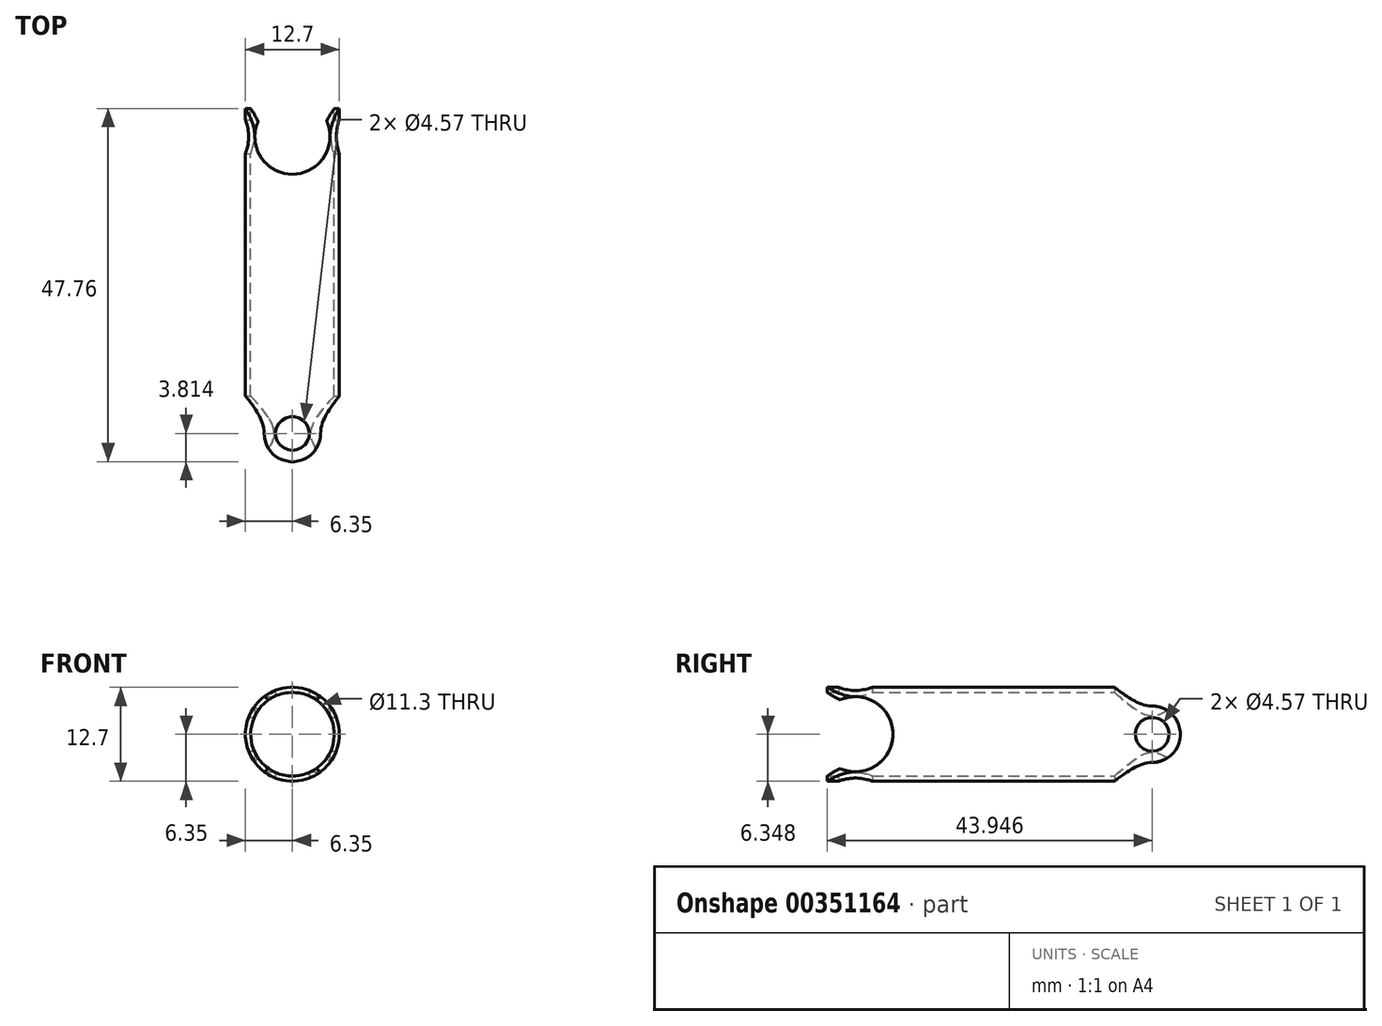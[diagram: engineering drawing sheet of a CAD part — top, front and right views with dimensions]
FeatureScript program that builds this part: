
annotation { "Feature Type Name" : "Feature", "Feature Type Description" : "" }
export const myFeature = defineFeature(function(context is Context, id is Id, definition is map)
    precondition{}
    {
        {
            var Q0;
            Q0=qCreatedBy(makeId("Front.planeOp"),FACE);
            var sketch = newSketch(context, id + "F0", { "sketchPlane" : qUnion([Q0])});
            skCircle(sketch, "E0", {"center": v(0, 0) * mm, "radius": 6.35 * mm});
            skCircle(sketch, "E1", {"center": v(0, 0) * mm, "radius": 5.65 * mm});
            skSolve(sketch);
        }
        {
            var Q0;
            Q0 = qSketchRegion(id + "F0", true);
            extrude(context, id + "F1", {"entities" : qUnion([Q0]), "depth" : 50.8 * mm});
        }
        {
            var Q0;
            Q0=qCreatedBy(makeId("Right.planeOp"),FACE);
            var sketch = newSketch(context, id + "F2", { "sketchPlane" : qUnion([Q0])});
            skCircle(sketch, "E2", {"center": v(-45.47, 0) * mm, "radius": 5.08 * mm});
            skCircle(sketch, "E3", {"center": v(-5.33, 0) * mm, "radius": 2.29 * mm});
            skSolve(sketch);
        }
        {
            var Q0;
            Q0 = qSketchRegion(id + "F2", true);
            extrude(context, id + "F3", {"entities" : qUnion([Q0]), "operationType" : NewBodyOperationType.REMOVE, "endBound" : BoundingType.SYMMETRIC, "oppositeDirection" : true, "depth" : 25.4 * mm});
        }
        {
            var Q0;
            Q0=qCreatedBy(makeId("Top.planeOp"),FACE);
            var sketch = newSketch(context, id + "F4", { "sketchPlane" : qUnion([Q0])});
            skCircle(sketch, "E4", {"center": v(0, -45.47) * mm, "radius": 2.29 * mm});
            skCircle(sketch, "E5", {"center": v(0, -5.33) * mm, "radius": 5.08 * mm});
            skSolve(sketch);
        }
        {
            var Q0;
            Q0 = qSketchRegion(id + "F4", true);
            extrude(context, id + "F5", {"entities" : qUnion([Q0]), "operationType" : NewBodyOperationType.REMOVE, "endBound" : BoundingType.SYMMETRIC, "depth" : 25.4 * mm});
        }
        {
            var Q0;
            Q0=qCreatedBy(makeId("Top.planeOp"),FACE);
            var sketch = newSketch(context, id + "F6", { "sketchPlane" : qUnion([Q0])});
            skArc(sketch, "E6", {"start": v(-3.81, -45.46) * mm, "mid": v(0, -49.28) * mm, "end": v(3.81, -45.47) * mm});
            skLineSegment(sketch, "E7.0", {"start": v(6.35, -50.8) * mm, "end": v(-6.35, -50.8) * mm});
            skLineSegment(sketch, "E8", {"start": v(-6.35, -50.8) * mm, "end": v(-6.35, -50.55) * mm});
            skLineSegment(sketch, "E9.trimOffspring", {"start": v(6.35, -50.55) * mm, "end": v(6.35, -50.8) * mm});
            skLineSegment(sketch, "E10", {"start": v(-3.81, -45.46) * mm, "end": v(-6.35, -45.46) * mm});
            skLineSegment(sketch, "E11", {"start": v(-6.35, -45.46) * mm, "end": v(-6.35, -50.55) * mm});
            skLineSegment(sketch, "E12", {"start": v(6.35, -50.55) * mm, "end": v(6.35, -45.47) * mm});
            skLineSegment(sketch, "E13", {"start": v(6.35, -45.47) * mm, "end": v(3.81, -45.47) * mm});
            skSolve(sketch);
        }
        {
            var Q0;
            Q0 = qSketchRegion(id + "F6", true);
            extrude(context, id + "F7", {"entities" : qUnion([Q0]), "operationType" : NewBodyOperationType.REMOVE, "endBound" : BoundingType.SYMMETRIC, "depth" : 25.4 * mm});
        }
        {
            var Q0;
            Q0=qCreatedBy(makeId("Right.planeOp"),FACE);
            var sketch = newSketch(context, id + "F8", { "sketchPlane" : qUnion([Q0])});
            skCircle(sketch, "E14", {"center": v(-5.33, 0) * mm, "radius": 2.29 * mm, "construction": true});
            skArc(sketch, "E15", {"start": v(-5.33, -3.81) * mm, "mid": v(-1.52, 0) * mm, "end": v(-5.33, 3.81) * mm});
            skLineSegment(sketch, "E16", {"start": v(-5.33, 7.72) * mm, "end": v(0, 7.72) * mm});
            skLineSegment(sketch, "E17", {"start": v(0, 7.72) * mm, "end": v(0, -7.2) * mm});
            skLineSegment(sketch, "E18", {"start": v(0, -7.2) * mm, "end": v(-5.33, -7.2) * mm});
            skLineSegment(sketch, "E19", {"start": v(-5.33, -7.2) * mm, "end": v(-5.33, -3.81) * mm});
            skLineSegment(sketch, "E20.trimOffspring", {"start": v(-5.33, 3.81) * mm, "end": v(-5.33, 7.72) * mm});
            skSolve(sketch);
        }
        {
            var Q0;
            Q0 = qSketchRegion(id + "F8", true);
            extrude(context, id + "F9", {"entities" : qUnion([Q0]), "operationType" : NewBodyOperationType.REMOVE, "endBound" : BoundingType.SYMMETRIC, "oppositeDirection" : true, "depth" : 25.4 * mm});
        }
    });
